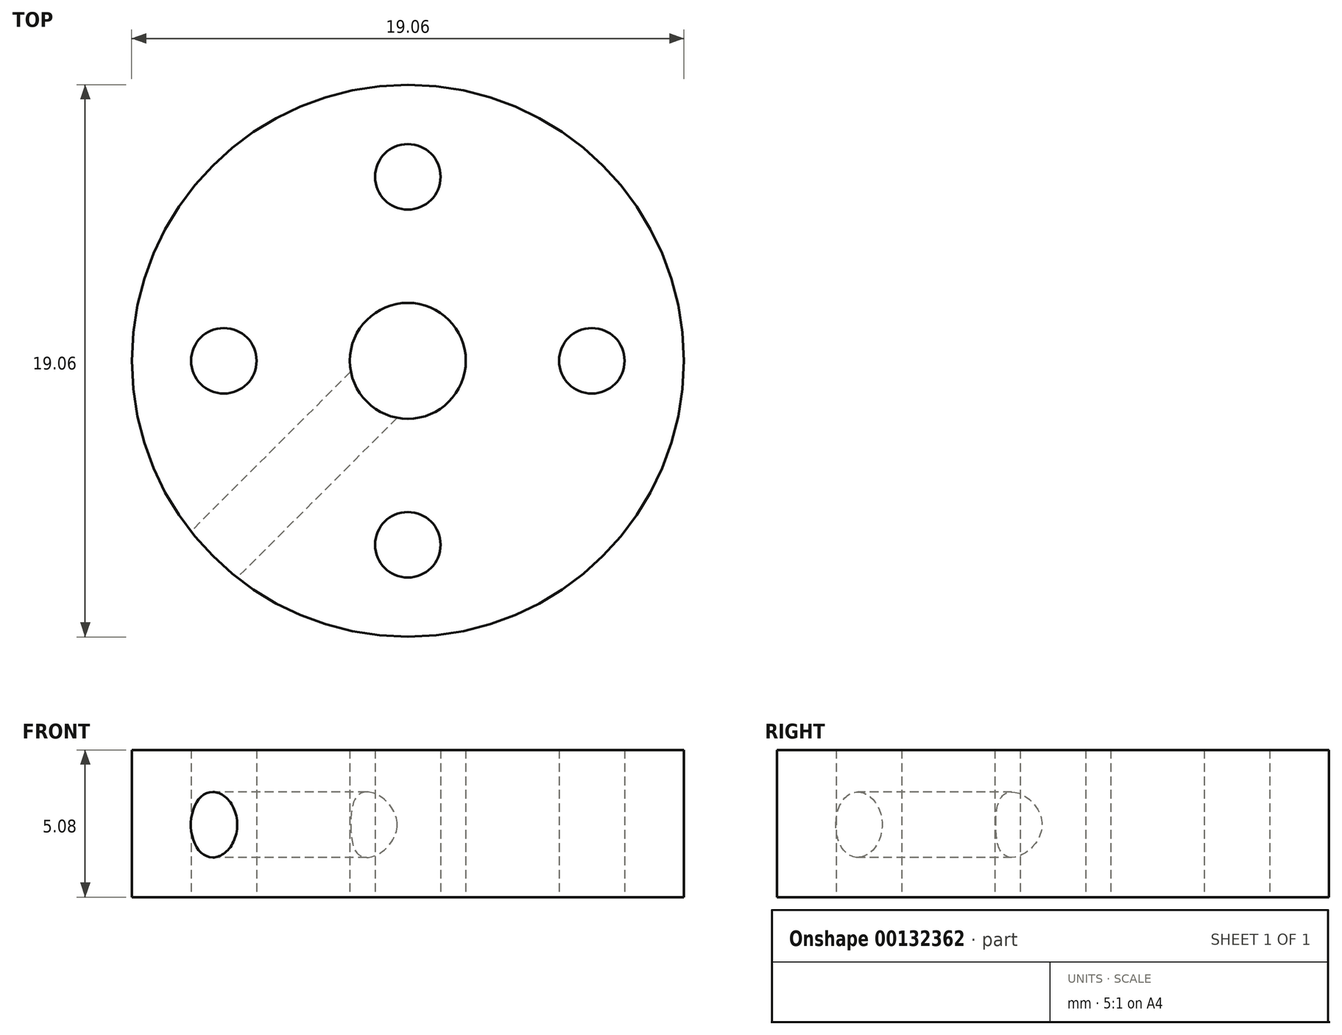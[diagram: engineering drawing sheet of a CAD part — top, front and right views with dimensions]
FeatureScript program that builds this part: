
annotation { "Feature Type Name" : "Feature", "Feature Type Description" : "" }
export const myFeature = defineFeature(function(context is Context, id is Id, definition is map)
    precondition{}
    {
        {
            var Q0;
            Q0=qCreatedBy(makeId("Top.planeOp"),FACE);
            var sketch = newSketch(context, id + "F0", { "sketchPlane" : qUnion([Q0])});
            skCircle(sketch, "E0", {"center": v(0, 0) * mm, "radius": 9.53 * mm});
            skCircle(sketch, "E1", {"center": v(0, 0) * mm, "radius": 2 * mm});
            skLineSegment(sketch, "E2", {"start": v(0, 0) * mm, "end": v(-6.74, -6.74) * mm});
            skLineSegment(sketch, "E3", {"start": v(0, 0) * mm, "end": v(0, -9.53) * mm});
            skLineSegment(sketch, "E4", {"start": v(0, 0) * mm, "end": v(0, 6.35) * mm});
            skLineSegment(sketch, "E5.1.0", {"start": v(0, 0) * mm, "end": v(-6.35, 0) * mm});
            skLineSegment(sketch, "E5.2.0", {"start": v(0, 0) * mm, "end": v(0, -6.35) * mm});
            skLineSegment(sketch, "E5.3.0", {"start": v(0, 0) * mm, "end": v(6.35, 0) * mm});
            skSolve(sketch);
        }
        {
            var Q0;
            {var subQ6=sQuery(id+"F0.wireOp",EDGE,"E3");Q0=makeQuery(id+"F0.imprint","IMPRINT",FACE,{"disambiguationData":[TD([[makeQuery(id+"F0.imprint","IMPRINT",EDGE,{"derivedFrom":subQ6}),1.0]])]});}
            var Q1;
            {var subQ0=sQuery(id+"F0.wireOp",EDGE,"E3");Q1=makeQuery(id+"F0.imprint","IMPRINT",FACE,{"disambiguationData":[TD([[makeQuery(id+"F0.imprint","IMPRINT",EDGE,{"derivedFrom":subQ0}),-1.0]])]});}
            extrude(context, id + "F1", {"entities" : qUnion([Q0, Q1]), "depth" : 5.08 * mm});
        }
        {
            var Q0;
            Q0=sQuery(id+"F0.wireOp",VERTEX,"E2.end");
            var Q1;
            Q1=sQuery(id+"F0.wireOp",EDGE,"E2");
            cPlane(context, id + "F2", {"entities" : qUnion([Q0, Q1]), "cplaneType" : CPlaneType.CURVE_POINT, "offset" : 25.4 * mm, "width" : 152.4 * mm, "height" : 152.4 * mm});
        }
        {
            var Q0;
            Q0=qCreatedBy(id+"F2.planeOp",FACE);
            var sketch = newSketch(context, id + "F3", { "sketchPlane" : qUnion([Q0])});
            skLineSegment(sketch, "E6", {"start": v(0, 0) * mm, "end": v(0, 2.5) * mm});
            skSolve(sketch);
        }
        {
            var Q0;
            Q0=sQuery(id+"F3.wireOp",VERTEX,"E6.end");
            var Q1;
            Q1=makeQuery(id+"F1.opExtrude","SWEPT_BODY",BODY,{"disambiguationData":[OSD([sQuery(id+"F0.wireOp",EDGE,"E0"),sQuery(id+"F0.wireOp",EDGE,"E1"),sQuery(id+"F0.wireOp",EDGE,"656e2fe9-e8eb-41f5-8be1-b4debb7fb939"),sQuery(id+"F0.wireOp",EDGE,"d9ba47e0-7eea-4d6b-86d8-9a2986d8aaf1.1.0"),sQuery(id+"F0.wireOp",EDGE,"d9ba47e0-7eea-4d6b-86d8-9a2986d8aaf1.2.0"),sQuery(id+"F0.wireOp",EDGE,"d9ba47e0-7eea-4d6b-86d8-9a2986d8aaf1.3.0")])]});
            hole(context, id + "F4", {"style" : HoleStyle.SIMPLE, "endStyle" : HoleEndStyle.BLIND, "standardTappedOrClearance" : lookupTablePath({ "standard" : "ANSI", "engagement" : "75%", "pitch" : "40 tpi", "size" : "#4", "type" : "Tapped" }), "standardBlindInLast" : lookupTablePath({ "standard" : "ANSI", "engagement" : "75%", "pitch" : "40 tpi", "size" : "#4", "type" : "Tapped" }), "holeDiameter" : 2.26 * mm, "holeDepth" : 9.52 * mm, "locations" : qUnion([Q0]), "scope" : qUnion([Q1]), "majorDiameter" : 2.84 * mm});
        }
        {
            var Q0;
            Q0=sQuery(id+"F0.wireOp",VERTEX,"E4.end");
            var Q1;
            Q1=sQuery(id+"F0.wireOp",VERTEX,"E5.3.0.end");
            var Q2;
            Q2=sQuery(id+"F0.wireOp",VERTEX,"E5.2.0.end");
            var Q3;
            Q3=sQuery(id+"F0.wireOp",VERTEX,"E5.1.0.end");
            var Q4;
            Q4=makeQuery(id+"F1.opExtrude","SWEPT_BODY",BODY,{"disambiguationData":[OSD([sQuery(id+"F0.wireOp",EDGE,"E0"),sQuery(id+"F0.wireOp",EDGE,"E1")])]});
            hole(context, id + "F5", {"style" : HoleStyle.SIMPLE, "endStyle" : HoleEndStyle.BLIND, "oppositeDirection" : true, "standardTappedOrClearance" : lookupTablePath({ "standard" : "ANSI", "engagement" : "75%", "pitch" : "40 tpi", "size" : "#4", "type" : "Tapped" }), "standardBlindInLast" : lookupTablePath({ "standard" : "ANSI", "engagement" : "75%", "pitch" : "40 tpi", "size" : "#4", "type" : "Tapped" }), "holeDiameter" : 2.26 * mm, "holeDepth" : 5.08 * mm, "locations" : qUnion([Q0, Q1, Q2, Q3]), "scope" : qUnion([Q4]), "majorDiameter" : 2.84 * mm});
        }
    });
